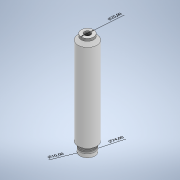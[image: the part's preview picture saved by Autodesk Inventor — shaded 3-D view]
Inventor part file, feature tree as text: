
AUTODESK INVENTOR PART (.ipt)
format: ipt  version: 2021 (Build 250183000, 183)  size: 145,408 bytes
history: native  units: mm
features: other x7, extrude x4, sketch x4, chamfer x2
ambient origin geometry x8: Origin, YZ Plane, XZ Plane, XY Plane, X Axis, Y Axis, Z Axis, Center Point
bodies: Solide1 (feature_tree)
feature tree (17):
  other  "Annotations"
  extrude  "Extrusion1"  Depth=30.0mm
  extrude  "Extrusion2"  Depth=150.0mm TaperAngle=0.0deg
  other  "Filetage2"
  chamfer  "Chanfrein1"  Distance=20.0mm
  chamfer  "Chanfrein2"  Distance=154.0mm
  extrude  "Extrusion4"  Depth=4.0mm TaperAngle=0.0deg
  extrude  "Extrusion3"  Depth=154.0mm TaperAngle=0.0deg
  other  "Filetage5"
  sketch  "Esquisse1"
  sketch  "Esquisse2"
  sketch  "Esquisse3"
  sketch  "Esquisse5"
  other  "Cote de diamètre 1"
  other  "Cote de diamètre 2"
  other  "Cote de diamètre 3"
  other  "Cote de diamètre 4"
